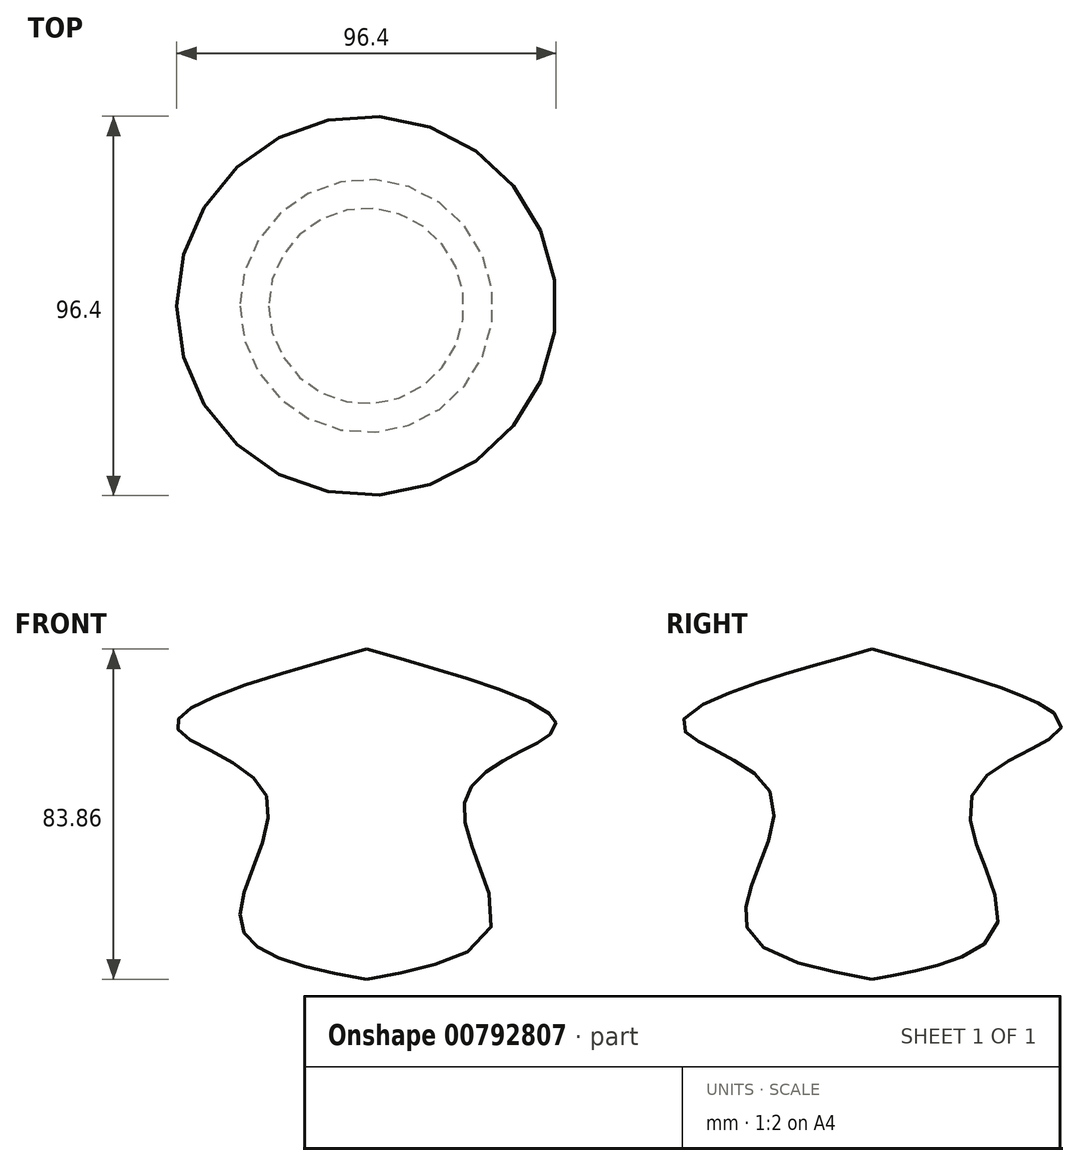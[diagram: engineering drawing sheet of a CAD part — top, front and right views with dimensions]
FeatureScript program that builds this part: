
annotation { "Feature Type Name" : "Feature", "Feature Type Description" : "" }
export const myFeature = defineFeature(function(context is Context, id is Id, definition is map)
    precondition{}
    {
        {
            var Q0;
            Q0=qCreatedBy(makeId("Front.planeOp"),FACE);
            var sketch = newSketch(context, id + "F0", { "sketchPlane" : qUnion([Q0])});
            skLineSegment(sketch, "E0", {"start": v(0, -47.17) * mm, "end": v(0, 36.69) * mm});
            skFitSpline(sketch, "E1", {"points": [v(0, 36.69) * mm, v(-48.02, 16.62) * mm, v(-25.65, 0) * mm, v(-32.04, -32.51) * mm, v(0, -47.17) * mm], "startDerivative": vector(-254.5, -70.75) * mm, "endDerivative": vector(187.23, -34.43) * mm});
            skSolve(sketch);
        }
        {
            var Q0;
            Q0 = qSketchRegion(id + "F0", true);
            var Q1;
            Q1=sQuery(id+"F0.wireOp",EDGE,"E0");
            revolve(context, id + "F1", {"surfaceOperationType" : NewSurfaceOperationType.NEW, "entities" : qUnion([Q0]), "axis" : qUnion([Q1]), "revolveType" : RevolveType.FULL});
        }
    });
